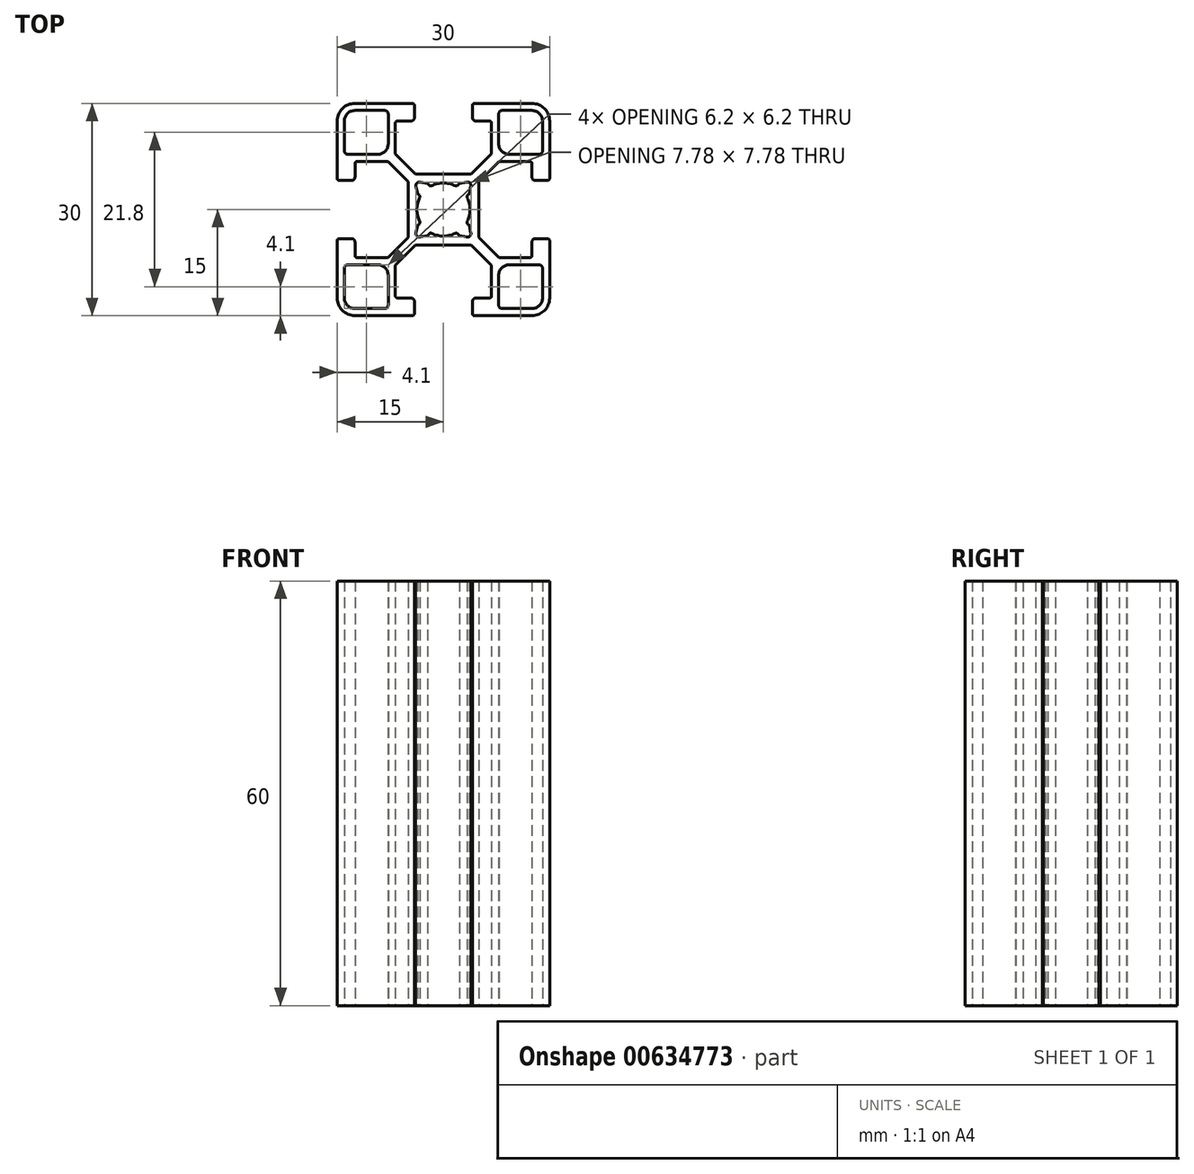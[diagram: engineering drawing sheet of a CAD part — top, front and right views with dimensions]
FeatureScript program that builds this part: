
annotation { "Feature Type Name" : "Feature", "Feature Type Description" : "" }
export const myFeature = defineFeature(function(context is Context, id is Id, definition is map)
    precondition{}
    {
        {
            var Q0;
            Q0=qCreatedBy(makeId("Top.planeOp"),FACE);
            var sketch = newSketch(context, id + "F0", { "sketchPlane" : qUnion([Q0])});
            skLineSegment(sketch, "E0", {"start": v(3.88, -3.29) * mm, "end": v(3.66, -2.24) * mm});
            skLineSegment(sketch, "E1", {"start": v(-3.66, 2.24) * mm, "end": v(-3.88, 3.29) * mm});
            skLineSegment(sketch, "E2", {"start": v(-2, 3.42) * mm, "end": v(-2.24, 3.66) * mm});
            skLineSegment(sketch, "E3", {"start": v(6.8, -7.86) * mm, "end": v(3.94, -5) * mm});
            skLineSegment(sketch, "E4", {"start": v(7.86, -6.8) * mm, "end": v(5, -3.94) * mm});
            skLineSegment(sketch, "E5", {"start": v(-3.42, 2) * mm, "end": v(-3.66, 2.24) * mm});
            skLineSegment(sketch, "E6", {"start": v(2.24, -3.66) * mm, "end": v(2, -3.42) * mm});
            skLineSegment(sketch, "E7", {"start": v(-5, 3.94) * mm, "end": v(-7.86, 6.8) * mm});
            skLineSegment(sketch, "E8", {"start": v(-3.94, 5) * mm, "end": v(-6.8, 7.86) * mm});
            skLineSegment(sketch, "E9", {"start": v(3.66, -2.24) * mm, "end": v(3.42, -2) * mm});
            skLineSegment(sketch, "E10", {"start": v(3.29, -3.88) * mm, "end": v(2.24, -3.66) * mm});
            skLineSegment(sketch, "E11", {"start": v(-2.24, 3.66) * mm, "end": v(-3.29, 3.88) * mm});
            skLineSegment(sketch, "E12", {"start": v(-12.5, -15) * mm, "end": v(-4.4, -15) * mm});
            skLineSegment(sketch, "E13", {"start": v(4.4, -15) * mm, "end": v(12.5, -15) * mm});
            skLineSegment(sketch, "E14", {"start": v(8.3, -14) * mm, "end": v(12.5, -14) * mm});
            skLineSegment(sketch, "E15", {"start": v(-12.5, -14) * mm, "end": v(-8.3, -14) * mm});
            skLineSegment(sketch, "E16", {"start": v(-6.5, -12.5) * mm, "end": v(-4.6, -12.5) * mm});
            skLineSegment(sketch, "E17", {"start": v(4.6, -12.5) * mm, "end": v(6.5, -12.5) * mm});
            skLineSegment(sketch, "E18", {"start": v(9.3, -7.8) * mm, "end": v(13.5, -7.8) * mm});
            skLineSegment(sketch, "E19", {"start": v(-13.5, -7.8) * mm, "end": v(-9.3, -7.8) * mm});
            skLineSegment(sketch, "E20", {"start": v(-12.2, -6.8) * mm, "end": v(-7.86, -6.8) * mm});
            skLineSegment(sketch, "E21", {"start": v(7.86, -6.8) * mm, "end": v(12.2, -6.8) * mm});
            skLineSegment(sketch, "E22", {"start": v(-3.94, -5) * mm, "end": v(3.94, -5) * mm});
            skLineSegment(sketch, "E23", {"start": v(-14.7, -4.1) * mm, "end": v(-13, -4.1) * mm});
            skLineSegment(sketch, "E24", {"start": v(13, -4.1) * mm, "end": v(14.7, -4.1) * mm});
            skLineSegment(sketch, "E25", {"start": v(-14.7, 4.1) * mm, "end": v(-13, 4.1) * mm});
            skLineSegment(sketch, "E26", {"start": v(13, 4.1) * mm, "end": v(14.7, 4.1) * mm});
            skLineSegment(sketch, "E27", {"start": v(-3.94, 5) * mm, "end": v(3.94, 5) * mm});
            skLineSegment(sketch, "E28", {"start": v(-12.2, 6.8) * mm, "end": v(-7.86, 6.8) * mm});
            skLineSegment(sketch, "E29", {"start": v(7.86, 6.8) * mm, "end": v(12.2, 6.8) * mm});
            skLineSegment(sketch, "E30", {"start": v(-13.5, 7.8) * mm, "end": v(-9.3, 7.8) * mm});
            skLineSegment(sketch, "E31", {"start": v(9.3, 7.8) * mm, "end": v(13.5, 7.8) * mm});
            skLineSegment(sketch, "E32", {"start": v(4.6, 12.5) * mm, "end": v(6.5, 12.5) * mm});
            skLineSegment(sketch, "E33", {"start": v(-6.5, 12.5) * mm, "end": v(-4.6, 12.5) * mm});
            skLineSegment(sketch, "E34", {"start": v(-12.5, 14) * mm, "end": v(-8.3, 14) * mm});
            skLineSegment(sketch, "E35", {"start": v(8.3, 14) * mm, "end": v(12.5, 14) * mm});
            skLineSegment(sketch, "E36", {"start": v(4.4, 15) * mm, "end": v(12.5, 15) * mm});
            skLineSegment(sketch, "E37", {"start": v(-12.5, 15) * mm, "end": v(-4.4, 15) * mm});
            skLineSegment(sketch, "E38", {"start": v(-3.29, -3.88) * mm, "end": v(-2.24, -3.66) * mm});
            skLineSegment(sketch, "E39", {"start": v(2.24, 3.66) * mm, "end": v(3.29, 3.88) * mm});
            skLineSegment(sketch, "E40", {"start": v(3.42, 2) * mm, "end": v(3.66, 2.24) * mm});
            skLineSegment(sketch, "E41", {"start": v(-6.8, -7.86) * mm, "end": v(-3.94, -5) * mm});
            skLineSegment(sketch, "E42", {"start": v(-7.86, -6.8) * mm, "end": v(-5, -3.94) * mm});
            skLineSegment(sketch, "E43", {"start": v(-2.24, -3.66) * mm, "end": v(-2, -3.42) * mm});
            skLineSegment(sketch, "E44", {"start": v(-3.66, -2.24) * mm, "end": v(-3.42, -2) * mm});
            skLineSegment(sketch, "E45", {"start": v(5, 3.94) * mm, "end": v(7.86, 6.8) * mm});
            skLineSegment(sketch, "E46", {"start": v(3.94, 5) * mm, "end": v(6.8, 7.86) * mm});
            skLineSegment(sketch, "E47", {"start": v(2, 3.42) * mm, "end": v(2.24, 3.66) * mm});
            skLineSegment(sketch, "E48", {"start": v(-3.88, -3.29) * mm, "end": v(-3.66, -2.24) * mm});
            skLineSegment(sketch, "E49", {"start": v(3.66, 2.24) * mm, "end": v(3.88, 3.29) * mm});
            skLineSegment(sketch, "E50", {"start": v(-15, 4.4) * mm, "end": v(-15, 12.5) * mm});
            skLineSegment(sketch, "E51", {"start": v(-15, -12.5) * mm, "end": v(-15, -4.4) * mm});
            skLineSegment(sketch, "E52", {"start": v(-14, 8.3) * mm, "end": v(-14, 12.5) * mm});
            skLineSegment(sketch, "E53", {"start": v(-14, -12.5) * mm, "end": v(-14, -8.3) * mm});
            skLineSegment(sketch, "E54", {"start": v(-12.5, -6.5) * mm, "end": v(-12.5, -4.6) * mm});
            skLineSegment(sketch, "E55", {"start": v(-12.5, 4.6) * mm, "end": v(-12.5, 6.5) * mm});
            skLineSegment(sketch, "E56", {"start": v(-7.8, 9.3) * mm, "end": v(-7.8, 13.5) * mm});
            skLineSegment(sketch, "E57", {"start": v(-7.8, -13.5) * mm, "end": v(-7.8, -9.3) * mm});
            skLineSegment(sketch, "E58", {"start": v(-6.8, -12.2) * mm, "end": v(-6.8, -7.86) * mm});
            skLineSegment(sketch, "E59", {"start": v(-6.8, 7.86) * mm, "end": v(-6.8, 12.2) * mm});
            skLineSegment(sketch, "E60", {"start": v(-5, -3.94) * mm, "end": v(-5, 3.94) * mm});
            skLineSegment(sketch, "E61", {"start": v(-4.1, -14.7) * mm, "end": v(-4.1, -13) * mm});
            skLineSegment(sketch, "E62", {"start": v(-4.1, 13) * mm, "end": v(-4.1, 14.7) * mm});
            skLineSegment(sketch, "E63", {"start": v(4.1, -14.7) * mm, "end": v(4.1, -13) * mm});
            skLineSegment(sketch, "E64", {"start": v(4.1, 13) * mm, "end": v(4.1, 14.7) * mm});
            skLineSegment(sketch, "E65", {"start": v(5, -3.94) * mm, "end": v(5, 3.94) * mm});
            skLineSegment(sketch, "E66", {"start": v(6.8, -12.2) * mm, "end": v(6.8, -7.86) * mm});
            skLineSegment(sketch, "E67", {"start": v(6.8, 7.86) * mm, "end": v(6.8, 12.2) * mm});
            skLineSegment(sketch, "E68", {"start": v(7.8, 9.3) * mm, "end": v(7.8, 13.5) * mm});
            skLineSegment(sketch, "E69", {"start": v(7.8, -13.5) * mm, "end": v(7.8, -9.3) * mm});
            skLineSegment(sketch, "E70", {"start": v(12.5, -6.5) * mm, "end": v(12.5, -4.6) * mm});
            skLineSegment(sketch, "E71", {"start": v(12.5, 4.6) * mm, "end": v(12.5, 6.5) * mm});
            skLineSegment(sketch, "E72", {"start": v(14, 8.3) * mm, "end": v(14, 12.5) * mm});
            skLineSegment(sketch, "E73", {"start": v(14, -12.5) * mm, "end": v(14, -8.3) * mm});
            skLineSegment(sketch, "E74", {"start": v(15, -12.5) * mm, "end": v(15, -4.4) * mm});
            skLineSegment(sketch, "E75", {"start": v(15, 4.4) * mm, "end": v(15, 12.5) * mm});
            skArc(sketch, "E76", {"start": v(-14.7, -4.1) * mm, "mid": v(-14.91, -4.19) * mm, "end": v(-15, -4.4) * mm});
            skArc(sketch, "E77", {"start": v(-15, 4.4) * mm, "mid": v(-14.91, 4.19) * mm, "end": v(-14.7, 4.1) * mm});
            skArc(sketch, "E78", {"start": v(-13.5, -7.8) * mm, "mid": v(-13.85, -7.95) * mm, "end": v(-14, -8.3) * mm});
            skArc(sketch, "E79", {"start": v(-14, 8.3) * mm, "mid": v(-13.85, 7.95) * mm, "end": v(-13.5, 7.8) * mm});
            skArc(sketch, "E80", {"start": v(-12.5, -4.6) * mm, "mid": v(-12.65, -4.25) * mm, "end": v(-13, -4.1) * mm});
            skArc(sketch, "E81", {"start": v(-13, 4.1) * mm, "mid": v(-12.65, 4.25) * mm, "end": v(-12.5, 4.6) * mm});
            skArc(sketch, "E82", {"start": v(-14, -12.5) * mm, "mid": v(-13.56, -13.56) * mm, "end": v(-12.5, -14) * mm});
            skArc(sketch, "E83", {"start": v(-15, -12.5) * mm, "mid": v(-14.27, -14.27) * mm, "end": v(-12.5, -15) * mm});
            skArc(sketch, "E84", {"start": v(-12.5, 14) * mm, "mid": v(-13.56, 13.56) * mm, "end": v(-14, 12.5) * mm});
            skArc(sketch, "E85", {"start": v(-12.5, 15) * mm, "mid": v(-14.27, 14.27) * mm, "end": v(-15, 12.5) * mm});
            skArc(sketch, "E86", {"start": v(-12.5, -6.5) * mm, "mid": v(-12.41, -6.71) * mm, "end": v(-12.2, -6.8) * mm});
            skArc(sketch, "E87", {"start": v(-12.2, 6.8) * mm, "mid": v(-12.41, 6.71) * mm, "end": v(-12.5, 6.5) * mm});
            skArc(sketch, "E88", {"start": v(-7.8, -9.3) * mm, "mid": v(-8.24, -8.24) * mm, "end": v(-9.3, -7.8) * mm});
            skArc(sketch, "E89", {"start": v(-9.3, 7.8) * mm, "mid": v(-8.24, 8.24) * mm, "end": v(-7.8, 9.3) * mm});
            skArc(sketch, "E90", {"start": v(-8.3, -14) * mm, "mid": v(-7.95, -13.85) * mm, "end": v(-7.8, -13.5) * mm});
            skArc(sketch, "E91", {"start": v(-7.8, 13.5) * mm, "mid": v(-7.95, 13.85) * mm, "end": v(-8.3, 14) * mm});
            skArc(sketch, "E92", {"start": v(-6.8, -12.2) * mm, "mid": v(-6.71, -12.41) * mm, "end": v(-6.5, -12.5) * mm});
            skArc(sketch, "E93", {"start": v(-6.5, 12.5) * mm, "mid": v(-6.71, 12.41) * mm, "end": v(-6.8, 12.2) * mm});
            skArc(sketch, "E94", {"start": v(-4.1, -13) * mm, "mid": v(-4.25, -12.65) * mm, "end": v(-4.6, -12.5) * mm});
            skArc(sketch, "E95", {"start": v(-4.6, 12.5) * mm, "mid": v(-4.25, 12.65) * mm, "end": v(-4.1, 13) * mm});
            skArc(sketch, "E96", {"start": v(-4.4, -15) * mm, "mid": v(-4.19, -14.91) * mm, "end": v(-4.1, -14.7) * mm});
            skArc(sketch, "E97", {"start": v(-4.1, 14.7) * mm, "mid": v(-4.19, 14.91) * mm, "end": v(-4.4, 15) * mm});
            skArc(sketch, "E98", {"start": v(-3.42, -2) * mm, "mid": v(-3.34, -1.84) * mm, "end": v(-3.36, -1.66) * mm});
            skArc(sketch, "E99", {"start": v(-3.36, 1.66) * mm, "mid": v(-3.34, 1.84) * mm, "end": v(-3.42, 2) * mm});
            skArc(sketch, "E100", {"start": v(-3.88, -3.29) * mm, "mid": v(-3.74, -3.74) * mm, "end": v(-3.29, -3.88) * mm});
            skArc(sketch, "E101", {"start": v(-3.29, 3.88) * mm, "mid": v(-3.74, 3.74) * mm, "end": v(-3.88, 3.29) * mm});
            skArc(sketch, "E102", {"start": v(-1.66, -3.36) * mm, "mid": v(-1.84, -3.34) * mm, "end": v(-2, -3.42) * mm});
            skArc(sketch, "E103", {"start": v(-2, 3.42) * mm, "mid": v(-1.84, 3.34) * mm, "end": v(-1.66, 3.36) * mm});
            skArc(sketch, "E104", {"start": v(-3.36, 1.66) * mm, "mid": v(-3.75, 0) * mm, "end": v(-3.36, -1.66) * mm});
            skArc(sketch, "E105", {"start": v(1.66, 3.36) * mm, "mid": v(0, 3.75) * mm, "end": v(-1.66, 3.36) * mm});
            skArc(sketch, "E106", {"start": v(3.36, -1.66) * mm, "mid": v(3.75, 0) * mm, "end": v(3.36, 1.66) * mm});
            skArc(sketch, "E107", {"start": v(-1.66, -3.36) * mm, "mid": v(0, -3.75) * mm, "end": v(1.66, -3.36) * mm});
            skArc(sketch, "E108", {"start": v(2, -3.42) * mm, "mid": v(1.84, -3.34) * mm, "end": v(1.66, -3.36) * mm});
            skArc(sketch, "E109", {"start": v(1.66, 3.36) * mm, "mid": v(1.84, 3.34) * mm, "end": v(2, 3.42) * mm});
            skArc(sketch, "E110", {"start": v(3.29, -3.88) * mm, "mid": v(3.74, -3.74) * mm, "end": v(3.88, -3.29) * mm});
            skArc(sketch, "E111", {"start": v(3.88, 3.29) * mm, "mid": v(3.74, 3.74) * mm, "end": v(3.29, 3.88) * mm});
            skArc(sketch, "E112", {"start": v(3.36, -1.66) * mm, "mid": v(3.34, -1.84) * mm, "end": v(3.42, -2) * mm});
            skArc(sketch, "E113", {"start": v(3.42, 2) * mm, "mid": v(3.34, 1.84) * mm, "end": v(3.36, 1.66) * mm});
            skArc(sketch, "E114", {"start": v(4.1, -14.7) * mm, "mid": v(4.19, -14.91) * mm, "end": v(4.4, -15) * mm});
            skArc(sketch, "E115", {"start": v(4.4, 15) * mm, "mid": v(4.19, 14.91) * mm, "end": v(4.1, 14.7) * mm});
            skArc(sketch, "E116", {"start": v(4.6, -12.5) * mm, "mid": v(4.25, -12.65) * mm, "end": v(4.1, -13) * mm});
            skArc(sketch, "E117", {"start": v(4.1, 13) * mm, "mid": v(4.25, 12.65) * mm, "end": v(4.6, 12.5) * mm});
            skArc(sketch, "E118", {"start": v(6.5, -12.5) * mm, "mid": v(6.71, -12.41) * mm, "end": v(6.8, -12.2) * mm});
            skArc(sketch, "E119", {"start": v(6.8, 12.2) * mm, "mid": v(6.71, 12.41) * mm, "end": v(6.5, 12.5) * mm});
            skArc(sketch, "E120", {"start": v(7.8, -13.5) * mm, "mid": v(7.95, -13.85) * mm, "end": v(8.3, -14) * mm});
            skArc(sketch, "E121", {"start": v(8.3, 14) * mm, "mid": v(7.95, 13.85) * mm, "end": v(7.8, 13.5) * mm});
            skArc(sketch, "E122", {"start": v(9.3, -7.8) * mm, "mid": v(8.24, -8.24) * mm, "end": v(7.8, -9.3) * mm});
            skArc(sketch, "E123", {"start": v(7.8, 9.3) * mm, "mid": v(8.24, 8.24) * mm, "end": v(9.3, 7.8) * mm});
            skArc(sketch, "E124", {"start": v(12.2, -6.8) * mm, "mid": v(12.41, -6.71) * mm, "end": v(12.5, -6.5) * mm});
            skArc(sketch, "E125", {"start": v(12.5, 6.5) * mm, "mid": v(12.41, 6.71) * mm, "end": v(12.2, 6.8) * mm});
            skArc(sketch, "E126", {"start": v(12.5, -14) * mm, "mid": v(13.56, -13.56) * mm, "end": v(14, -12.5) * mm});
            skArc(sketch, "E127", {"start": v(12.5, -15) * mm, "mid": v(14.27, -14.27) * mm, "end": v(15, -12.5) * mm});
            skArc(sketch, "E128", {"start": v(14, 12.5) * mm, "mid": v(13.56, 13.56) * mm, "end": v(12.5, 14) * mm});
            skArc(sketch, "E129", {"start": v(15, 12.5) * mm, "mid": v(14.27, 14.27) * mm, "end": v(12.5, 15) * mm});
            skArc(sketch, "E130", {"start": v(13, -4.1) * mm, "mid": v(12.65, -4.25) * mm, "end": v(12.5, -4.6) * mm});
            skArc(sketch, "E131", {"start": v(12.5, 4.6) * mm, "mid": v(12.65, 4.25) * mm, "end": v(13, 4.1) * mm});
            skArc(sketch, "E132", {"start": v(14, -8.3) * mm, "mid": v(13.85, -7.95) * mm, "end": v(13.5, -7.8) * mm});
            skArc(sketch, "E133", {"start": v(13.5, 7.8) * mm, "mid": v(13.85, 7.95) * mm, "end": v(14, 8.3) * mm});
            skArc(sketch, "E134", {"start": v(15, -4.4) * mm, "mid": v(14.91, -4.19) * mm, "end": v(14.7, -4.1) * mm});
            skArc(sketch, "E135", {"start": v(14.7, 4.1) * mm, "mid": v(14.91, 4.19) * mm, "end": v(15, 4.4) * mm});
            skLineSegment(sketch, "E136", {"start": v(15, 4.4) * mm, "end": v(15, -4.4) * mm});
            skSolve(sketch);
        }
        {
            var Q0;
            Q0=makeQuery(id+"F0.imprint","IMPRINT",FACE,{"disambiguationData":[TD([[makeQuery(id+"F0.imprint","IMPRINT",EDGE,{"derivedFrom":sQuery(id+"F0.wireOp",EDGE,"E0")}),-1.0]])]});
            extrude(context, id + "F1", {"entities" : qUnion([Q0]), "depth" : 60 * mm, "offsetDistance" : 25 * mm});
        }
        {
            var Q0;
            Q0=sQuery(id+"F0.wireOp",EDGE,"E136");
            var Q1;
            Q1=makeQuery(id+"F1.opExtrude","CAP_FACE",FACE,{"disambiguationData":[OSD([sQuery(id+"F0.wireOp",EDGE,"E0"),sQuery(id+"F0.wireOp",EDGE,"E1"),sQuery(id+"F0.wireOp",EDGE,"E2"),sQuery(id+"F0.wireOp",EDGE,"E3"),sQuery(id+"F0.wireOp",EDGE,"E4"),sQuery(id+"F0.wireOp",EDGE,"E5"),sQuery(id+"F0.wireOp",EDGE,"E6"),sQuery(id+"F0.wireOp",EDGE,"E7"),sQuery(id+"F0.wireOp",EDGE,"E8"),sQuery(id+"F0.wireOp",EDGE,"E9"),sQuery(id+"F0.wireOp",EDGE,"E10"),sQuery(id+"F0.wireOp",EDGE,"E11"),sQuery(id+"F0.wireOp",EDGE,"E12"),sQuery(id+"F0.wireOp",EDGE,"E13"),sQuery(id+"F0.wireOp",EDGE,"E14"),sQuery(id+"F0.wireOp",EDGE,"E15"),sQuery(id+"F0.wireOp",EDGE,"E16"),sQuery(id+"F0.wireOp",EDGE,"E17"),sQuery(id+"F0.wireOp",EDGE,"E18"),sQuery(id+"F0.wireOp",EDGE,"E19"),sQuery(id+"F0.wireOp",EDGE,"E20"),sQuery(id+"F0.wireOp",EDGE,"E21"),sQuery(id+"F0.wireOp",EDGE,"E22"),sQuery(id+"F0.wireOp",EDGE,"E23"),sQuery(id+"F0.wireOp",EDGE,"E24"),sQuery(id+"F0.wireOp",EDGE,"E25"),sQuery(id+"F0.wireOp",EDGE,"E26"),sQuery(id+"F0.wireOp",EDGE,"E27"),sQuery(id+"F0.wireOp",EDGE,"E28"),sQuery(id+"F0.wireOp",EDGE,"E29"),sQuery(id+"F0.wireOp",EDGE,"E30"),sQuery(id+"F0.wireOp",EDGE,"E31"),sQuery(id+"F0.wireOp",EDGE,"E32"),sQuery(id+"F0.wireOp",EDGE,"E33"),sQuery(id+"F0.wireOp",EDGE,"E34"),sQuery(id+"F0.wireOp",EDGE,"E35"),sQuery(id+"F0.wireOp",EDGE,"E36"),sQuery(id+"F0.wireOp",EDGE,"E37"),sQuery(id+"F0.wireOp",EDGE,"E38"),sQuery(id+"F0.wireOp",EDGE,"E39"),sQuery(id+"F0.wireOp",EDGE,"E40"),sQuery(id+"F0.wireOp",EDGE,"E41"),sQuery(id+"F0.wireOp",EDGE,"E42"),sQuery(id+"F0.wireOp",EDGE,"E43"),sQuery(id+"F0.wireOp",EDGE,"E44"),sQuery(id+"F0.wireOp",EDGE,"E45"),sQuery(id+"F0.wireOp",EDGE,"E46"),sQuery(id+"F0.wireOp",EDGE,"E47"),sQuery(id+"F0.wireOp",EDGE,"E48"),sQuery(id+"F0.wireOp",EDGE,"E49"),sQuery(id+"F0.wireOp",EDGE,"E50"),sQuery(id+"F0.wireOp",EDGE,"E51"),sQuery(id+"F0.wireOp",EDGE,"E52"),sQuery(id+"F0.wireOp",EDGE,"E53"),sQuery(id+"F0.wireOp",EDGE,"E54"),sQuery(id+"F0.wireOp",EDGE,"E55"),sQuery(id+"F0.wireOp",EDGE,"E56"),sQuery(id+"F0.wireOp",EDGE,"E57"),sQuery(id+"F0.wireOp",EDGE,"E58"),sQuery(id+"F0.wireOp",EDGE,"E59"),sQuery(id+"F0.wireOp",EDGE,"E60"),sQuery(id+"F0.wireOp",EDGE,"E61"),sQuery(id+"F0.wireOp",EDGE,"E62"),sQuery(id+"F0.wireOp",EDGE,"E63"),sQuery(id+"F0.wireOp",EDGE,"E64"),sQuery(id+"F0.wireOp",EDGE,"E65"),sQuery(id+"F0.wireOp",EDGE,"E66"),sQuery(id+"F0.wireOp",EDGE,"E67"),sQuery(id+"F0.wireOp",EDGE,"E68"),sQuery(id+"F0.wireOp",EDGE,"E69"),sQuery(id+"F0.wireOp",EDGE,"E70"),sQuery(id+"F0.wireOp",EDGE,"E71"),sQuery(id+"F0.wireOp",EDGE,"E72"),sQuery(id+"F0.wireOp",EDGE,"E73"),sQuery(id+"F0.wireOp",EDGE,"E74"),sQuery(id+"F0.wireOp",EDGE,"E75"),sQuery(id+"F0.wireOp",EDGE,"E76"),sQuery(id+"F0.wireOp",EDGE,"E77"),sQuery(id+"F0.wireOp",EDGE,"E78"),sQuery(id+"F0.wireOp",EDGE,"E79"),sQuery(id+"F0.wireOp",EDGE,"E80"),sQuery(id+"F0.wireOp",EDGE,"E81"),sQuery(id+"F0.wireOp",EDGE,"E82"),sQuery(id+"F0.wireOp",EDGE,"E83"),sQuery(id+"F0.wireOp",EDGE,"E84"),sQuery(id+"F0.wireOp",EDGE,"E85"),sQuery(id+"F0.wireOp",EDGE,"E86"),sQuery(id+"F0.wireOp",EDGE,"E87"),sQuery(id+"F0.wireOp",EDGE,"E88"),sQuery(id+"F0.wireOp",EDGE,"E89"),sQuery(id+"F0.wireOp",EDGE,"E90"),sQuery(id+"F0.wireOp",EDGE,"E91"),sQuery(id+"F0.wireOp",EDGE,"E92"),sQuery(id+"F0.wireOp",EDGE,"E93"),sQuery(id+"F0.wireOp",EDGE,"E94"),sQuery(id+"F0.wireOp",EDGE,"E95"),sQuery(id+"F0.wireOp",EDGE,"E96"),sQuery(id+"F0.wireOp",EDGE,"E97"),sQuery(id+"F0.wireOp",EDGE,"E98"),sQuery(id+"F0.wireOp",EDGE,"E99"),sQuery(id+"F0.wireOp",EDGE,"E100"),sQuery(id+"F0.wireOp",EDGE,"E101"),sQuery(id+"F0.wireOp",EDGE,"E102"),sQuery(id+"F0.wireOp",EDGE,"E103"),sQuery(id+"F0.wireOp",EDGE,"E104"),sQuery(id+"F0.wireOp",EDGE,"E105"),sQuery(id+"F0.wireOp",EDGE,"E106"),sQuery(id+"F0.wireOp",EDGE,"E107"),sQuery(id+"F0.wireOp",EDGE,"E108"),sQuery(id+"F0.wireOp",EDGE,"E109"),sQuery(id+"F0.wireOp",EDGE,"E110"),sQuery(id+"F0.wireOp",EDGE,"E111"),sQuery(id+"F0.wireOp",EDGE,"E112"),sQuery(id+"F0.wireOp",EDGE,"E113"),sQuery(id+"F0.wireOp",EDGE,"E114"),sQuery(id+"F0.wireOp",EDGE,"E115"),sQuery(id+"F0.wireOp",EDGE,"E116"),sQuery(id+"F0.wireOp",EDGE,"E117"),sQuery(id+"F0.wireOp",EDGE,"E118"),sQuery(id+"F0.wireOp",EDGE,"E119"),sQuery(id+"F0.wireOp",EDGE,"E120"),sQuery(id+"F0.wireOp",EDGE,"E121"),sQuery(id+"F0.wireOp",EDGE,"E122"),sQuery(id+"F0.wireOp",EDGE,"E123"),sQuery(id+"F0.wireOp",EDGE,"E124"),sQuery(id+"F0.wireOp",EDGE,"E125"),sQuery(id+"F0.wireOp",EDGE,"E126"),sQuery(id+"F0.wireOp",EDGE,"E127"),sQuery(id+"F0.wireOp",EDGE,"E128"),sQuery(id+"F0.wireOp",EDGE,"E129"),sQuery(id+"F0.wireOp",EDGE,"E130"),sQuery(id+"F0.wireOp",EDGE,"E131"),sQuery(id+"F0.wireOp",EDGE,"E132"),sQuery(id+"F0.wireOp",EDGE,"E133"),sQuery(id+"F0.wireOp",EDGE,"E134"),sQuery(id+"F0.wireOp",EDGE,"E135")])],"isStart":false});
            extrude(context, id + "F2", {"bodyType" : ExtendedToolBodyType.SURFACE, "surfaceEntities" : qUnion([Q0]), "endBound" : BoundingType.UP_TO_SURFACE, "depth" : 25 * mm, "endBoundEntityFace" : qUnion([Q1]), "offsetDistance" : 25 * mm});
        }
    });
